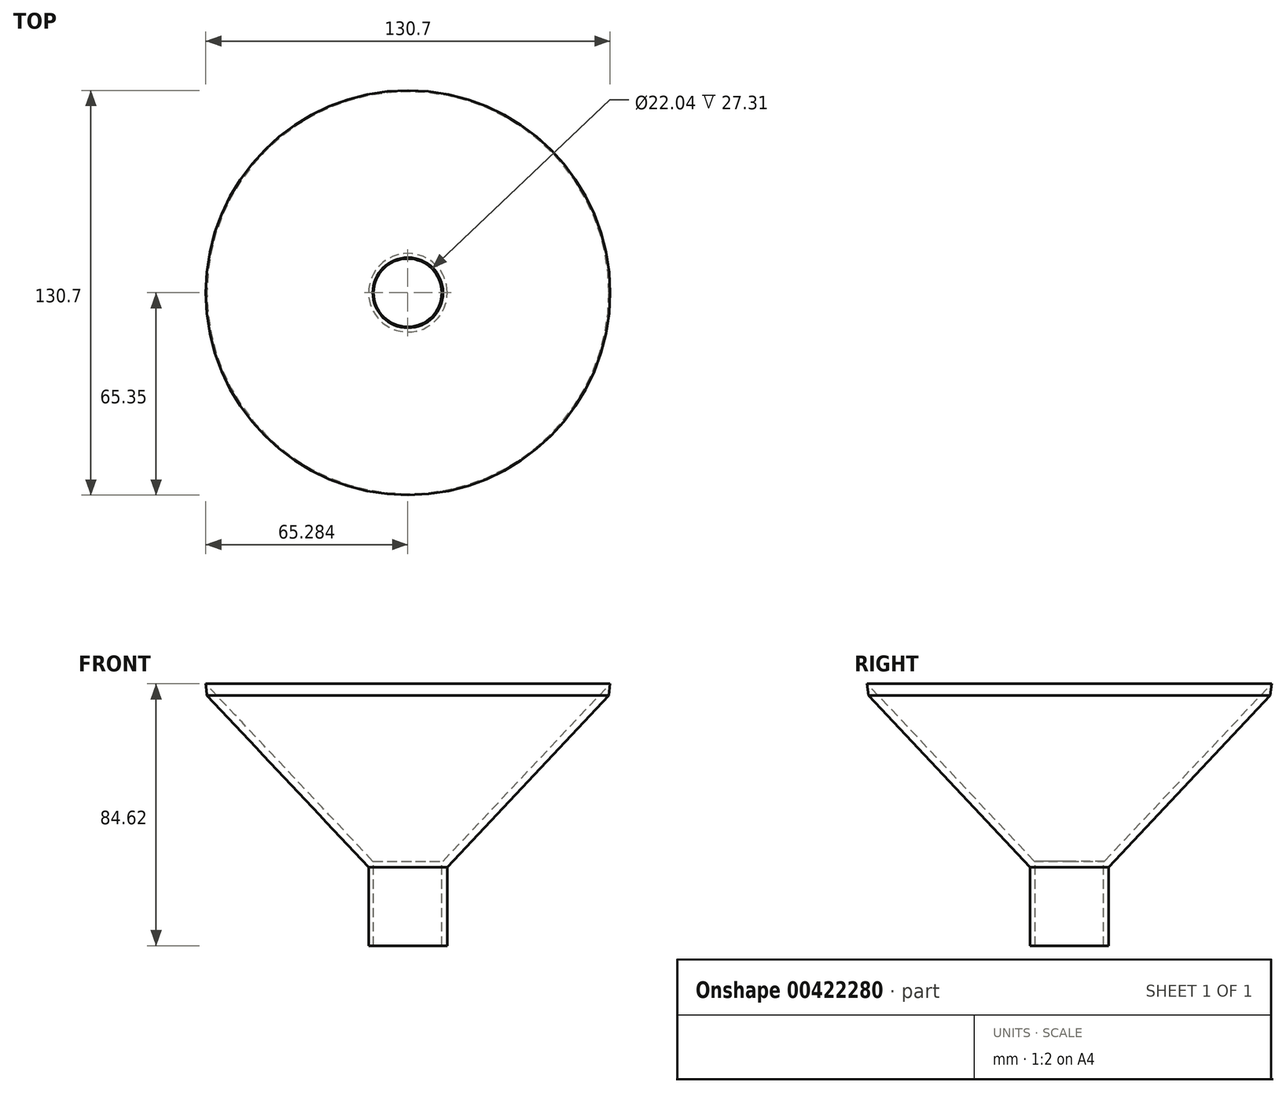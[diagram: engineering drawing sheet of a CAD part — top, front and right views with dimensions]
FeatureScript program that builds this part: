
annotation { "Feature Type Name" : "Feature", "Feature Type Description" : "" }
export const myFeature = defineFeature(function(context is Context, id is Id, definition is map)
    precondition{}
    {
        {
            var Q0;
            Q0=qCreatedBy(makeId("Front.planeOp"),FACE);
            var sketch = newSketch(context, id + "F0", { "sketchPlane" : qUnion([Q0])});
            skLineSegment(sketch, "E0", {"start": v(0, 0) * mm, "end": v(52.25, 55.46) * mm});
            skLineSegment(sketch, "E1", {"start": v(0, 0) * mm, "end": v(0, -25.4) * mm});
            skLineSegment(sketch, "E2", {"start": v(0, -25.4) * mm, "end": v(-12.7, -25.4) * mm});
            skLineSegment(sketch, "E3", {"start": v(-12.7, -25.4) * mm, "end": v(-12.7, 1.9) * mm});
            skLineSegment(sketch, "E4", {"start": v(-12.7, 1.9) * mm, "end": v(-1.34, 1.9) * mm});
            skLineSegment(sketch, "E5", {"start": v(-1.34, 1.9) * mm, "end": v(52.65, 59.22) * mm});
            skLineSegment(sketch, "E6", {"start": v(52.65, 59.22) * mm, "end": v(52.25, 55.46) * mm});
            skSolve(sketch);
        }
        {
            var Q0;
            Q0=makeQuery(id+"F0.imprint","IMPRINT",FACE,{"disambiguationData":[TD([[makeQuery(id+"F0.imprint","IMPRINT",EDGE,{"derivedFrom":sQuery(id+"F0.wireOp",EDGE,"E0")}),1.0]])]});
            var Q1;
            Q1=sQuery(id+"F0.wireOp",EDGE,"E3");
            revolve(context, id + "F1", {"entities" : qUnion([Q0]), "axis" : qUnion([Q1]), "revolveType" : RevolveType.FULL});
        }
        {
            var Q0;
            Q0=qCreatedBy(makeId("Top.planeOp"),FACE);
            var sketch = newSketch(context, id + "F2", { "sketchPlane" : qUnion([Q0])});
            skCircle(sketch, "E7", {"center": v(-12.77, 0) * mm, "radius": 11.02 * mm});
            skSolve(sketch);
        }
        {
            var Q0;
            Q0 = qSketchRegion(id + "F2", true);
            extrude(context, id + "F3", {"entities" : qUnion([Q0]), "operationType" : NewBodyOperationType.REMOVE, "oppositeDirection" : true, "depth" : 50.8 * mm});
        }
        {
            var Q0;
            Q0 = qSketchRegion(id + "F2", true);
            extrude(context, id + "F4", {"entities" : qUnion([Q0]), "operationType" : NewBodyOperationType.REMOVE, "oppositeDirection" : true, "depth" : -25.4 * mm});
        }
    });
